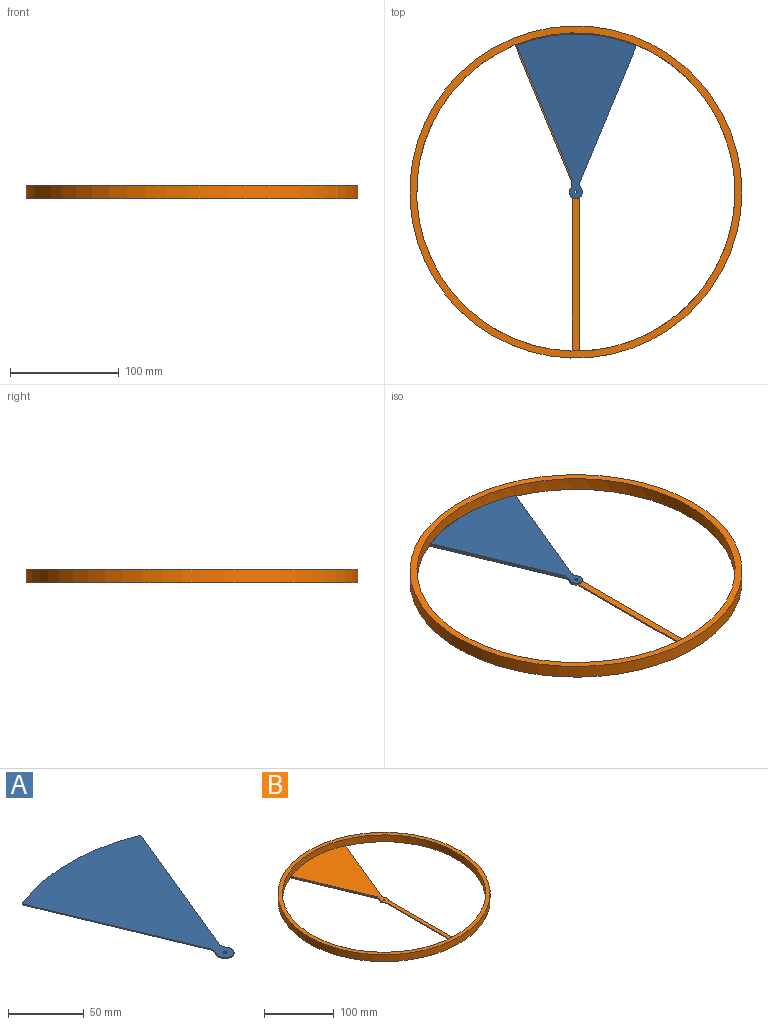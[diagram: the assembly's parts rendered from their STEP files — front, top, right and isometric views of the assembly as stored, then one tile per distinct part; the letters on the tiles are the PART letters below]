
ASSEMBLY  parts=2 mates=1
PART A: 12 faces, bbox 111x151.1x2 mm
  f0: plane 124.22x51.45mm, normal (0.92,-0.38,0), area 268.9mm2, adj f1,f5,f6,f10,f11
  f1: cylinder r=145.05mm len=111.02mm, axis (0,0,-1), area 92.6mm2, adj f0,f2,f6,f7,f9,f11
  f2: plane 124.22x51.45mm, normal (-0.92,-0.38,0), area 107.6mm2, adj f1,f3,f6,f7
  f3: cylinder r=6.35mm len=6.21mm, axis (0,0,-1), area 5.2mm2, adj f2,f4,f6,f7
  f4: cylinder r=6mm len=12mm, axis (0,0,-1), area 21.2mm2, adj f3,f5,f6,f7
  f5: cylinder r=6.35mm len=6.21mm, axis (0,0,-1), area 5.2mm2, adj f0,f4,f6,f7
  f6: plane 151.05x111.02mm, normal (0,0,1), area 8362.9mm2, adj f0,f1,f2,f3,f4,f5,f8
  f7: plane 151.05x109.91mm, normal (0,0,-1), area 8201.5mm2, adj f1,f2,f3,f4,f5,f8,f9,f10
  f8: cylinder r=1.2mm len=2.4mm, axis (0,0,-1), area 6mm2, adj f6,f7
  f9: plane 124.22x51.45mm, normal (-0.92,0.38,0), area 161.3mm2, adj f1,f7,f10,f11
  f10: plane 1.2x1.11mm, normal (-0.38,-0.92,0), area 1.4mm2, adj f0,f7,f9,f11
  f11: plane 124.68x52.56mm, normal (0,0,-1), area 161.3mm2, adj f0,f1,f9,f10
PART B: 17 faces, bbox 304.8x304.8x12 mm
  f0: cylinder r=146.05mm len=292.1mm, axis (0,0,-1), area 10865.2mm2, adj f2,f3,f4,f5,f8,f9,f12,f14
  f1: cylinder r=152.4mm len=304.8mm, axis (0,0,-1), area 11490.7mm2, adj f2,f3
  f2: plane 304.8x304.8mm, normal (0,0,1), area 5953.8mm2, adj f0,f1
  f3: plane 304.8x304.8mm, normal (0,0,-1), area 15322.1mm2, adj f0,f1,f4,f5,f6,f7,f8,f9
  f4: plane 125.15x51.84mm, normal (0.92,-0.38,0), area 162.5mm2, adj f0,f3,f11,f12
  f5: plane 125.15x51.84mm, normal (-0.92,-0.38,0), area 325.1mm2, adj f0,f3,f6,f13,f15
  f6: cylinder r=6.35mm len=6.21mm, axis (0,0,-1), area 7.9mm2, adj f3,f5,f7,f12
  f7: cylinder r=6mm len=8.67mm, axis (0,0,-1), area 11.9mm2, adj f3,f6,f8,f12
  f8: plane 140.92x1.2mm, normal (-1,0,0), area 169.1mm2, adj f0,f3,f7,f12
  f9: plane 140.92x1.2mm, normal (1,0,0), area 169.1mm2, adj f0,f3,f10,f12
  f10: cylinder r=6mm len=8.67mm, axis (0,0,-1), area 11.9mm2, adj f3,f9,f11,f12
  f11: cylinder r=6.35mm len=6.21mm, axis (0,0,-1), area 7.9mm2, adj f3,f4,f10,f12
  f12: plane 292.1x110.67mm, normal (0,0,1), area 9205.8mm2, adj f0,f4,f6,f7,f8,f9,f10,f11
  f13: plane 1.2x1.11mm, normal (0.38,-0.92,0), area 1.4mm2, adj f5,f12,f14,f15
  f14: plane 125.14x51.84mm, normal (0.92,0.38,0), area 162.5mm2, adj f0,f12,f13,f15
  f15: plane 125.6x52.95mm, normal (0,0,1), area 162.5mm2, adj f0,f5,f13,f14
  f16: cylinder r=1.2mm len=2.4mm, axis (0,0,1), area 9mm2, adj f3,f12
PLACE A t=(-1.18,1.42,-4.25)mm
PLACE B t=(-1.18,1.42,-2.85)mm
MATE revolute A.f8 <-> B.f7  axis (0,0,-1) through (-1.18,1.42,-1.65)mm
